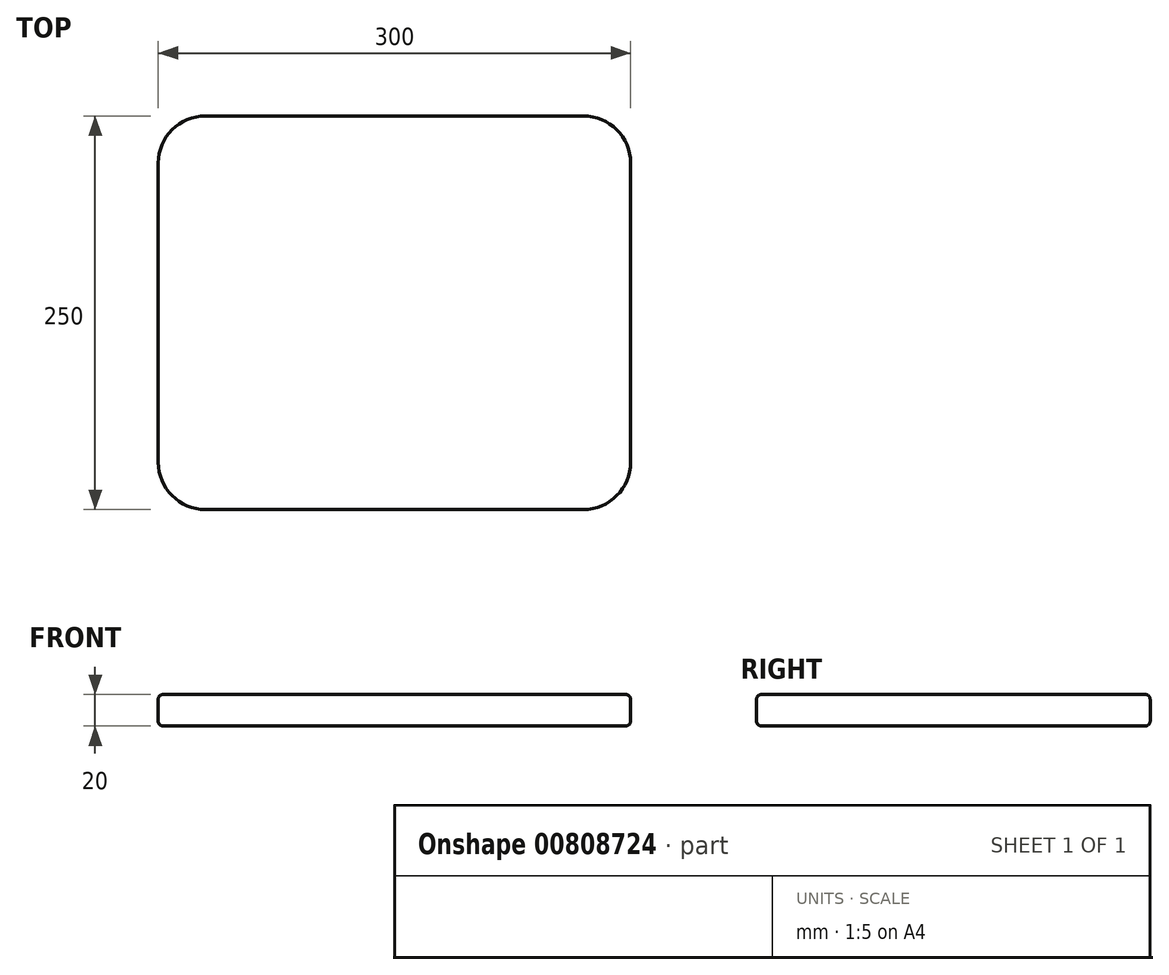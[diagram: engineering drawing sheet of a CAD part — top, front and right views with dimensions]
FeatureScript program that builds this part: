
annotation { "Feature Type Name" : "Feature", "Feature Type Description" : "" }
export const myFeature = defineFeature(function(context is Context, id is Id, definition is map)
    precondition{}
    {
        {
            var Q0;
            Q0=qCreatedBy(makeId("Top.planeOp"),FACE);
            var sketch = newSketch(context, id + "F0", { "sketchPlane" : qUnion([Q0])});
            skLineSegment(sketch, "E0.bottom", {"start": v(-113.42, 89.43) * mm, "end": v(126.58, 89.43) * mm});
            skLineSegment(sketch, "E0.top", {"start": v(-113.42, -160.57) * mm, "end": v(126.58, -160.57) * mm});
            skLineSegment(sketch, "E0.left", {"start": v(-143.42, 59.43) * mm, "end": v(-143.42, -130.57) * mm});
            skLineSegment(sketch, "E0.right", {"start": v(156.58, 59.43) * mm, "end": v(156.58, -130.57) * mm});
            skPoint(sketch, "E1.visualSharp", {"position": v(-143.42, 89.43) * mm});
            skArc(sketch, "E1.filletArc", {"start": v(-113.42, 89.43) * mm, "mid": v(-134.63, 80.65) * mm, "end": v(-143.42, 59.43) * mm});
            skPoint(sketch, "E2.visualSharp", {"position": v(156.58, 89.43) * mm});
            skArc(sketch, "E2.filletArc", {"start": v(156.58, 59.43) * mm, "mid": v(147.8, 80.65) * mm, "end": v(126.58, 89.43) * mm});
            skPoint(sketch, "E3.visualSharp", {"position": v(156.58, -160.57) * mm});
            skArc(sketch, "E3.filletArc", {"start": v(126.58, -160.57) * mm, "mid": v(147.8, -151.78) * mm, "end": v(156.58, -130.57) * mm});
            skPoint(sketch, "E4.visualSharp", {"position": v(-143.42, -160.57) * mm});
            skArc(sketch, "E4.filletArc", {"start": v(-143.42, -130.57) * mm, "mid": v(-134.63, -151.78) * mm, "end": v(-113.42, -160.57) * mm});
            skSolve(sketch);
        }
        {
            var Q0;
            Q0=makeQuery(id+"F0.imprint","IMPRINT",FACE,{"disambiguationData":[TD([[makeQuery(id+"F0.imprint","IMPRINT",EDGE,{"derivedFrom":sQuery(id+"F0.wireOp",EDGE,"E0.bottom")}),-1.0]])]});
            extrude(context, id + "F1", {"entities" : qUnion([Q0]), "depth" : 20 * mm, "offsetDistance" : 25 * mm});
        }
        {
            var Q0;
            Q0=makeQuery(id+"F1.opExtrude","CAP_FACE",FACE,{"disambiguationData":[OSD([sQuery(id+"F0.wireOp",EDGE,"E0.bottom"),sQuery(id+"F0.wireOp",EDGE,"E0.top"),sQuery(id+"F0.wireOp",EDGE,"E0.left"),sQuery(id+"F0.wireOp",EDGE,"E0.right"),sQuery(id+"F0.wireOp",EDGE,"E1.filletArc"),sQuery(id+"F0.wireOp",EDGE,"E2.filletArc"),sQuery(id+"F0.wireOp",EDGE,"E3.filletArc"),sQuery(id+"F0.wireOp",EDGE,"E4.filletArc")])],"isStart":false});
            var Q1;
            Q1=makeQuery(id+"F1.opExtrude","CAP_FACE",FACE,{"disambiguationData":[OSD([sQuery(id+"F0.wireOp",EDGE,"E0.bottom"),sQuery(id+"F0.wireOp",EDGE,"E0.top"),sQuery(id+"F0.wireOp",EDGE,"E0.left"),sQuery(id+"F0.wireOp",EDGE,"E0.right"),sQuery(id+"F0.wireOp",EDGE,"E1.filletArc"),sQuery(id+"F0.wireOp",EDGE,"E2.filletArc"),sQuery(id+"F0.wireOp",EDGE,"E3.filletArc"),sQuery(id+"F0.wireOp",EDGE,"E4.filletArc")])],"isStart":true});
            fillet(context, id + "F2", {"entities" : qUnion([Q0, Q1]), "radius" : 3 * mm, "tangentPropagation" : true, "allowEdgeOverflow" : false});
        }
        {
            var Q0;
            Q0=makeQuery(id+"F1.opExtrude","SWEPT_FACE",FACE,{"disambiguationData":[OSD([sQuery(id+"F0.wireOp",EDGE,"E0.left")])]});
            var sketch = newSketch(context, id + "F3", { "sketchPlane" : qUnion([Q0])});
            skLineSegment(sketch, "E5.0", {"start": v(-89.43, 17) * mm, "end": v(-89.43, 3) * mm, "construction": true});
            skLineSegment(sketch, "E6", {"start": v(-89.43, 10) * mm, "end": v(-59.43, 10) * mm, "construction": true});
            skLineSegment(sketch, "E7", {"start": v(-59.43, 10) * mm, "end": v(-29.43, 10) * mm, "construction": true});
            skLineSegment(sketch, "E8", {"start": v(-29.43, 10) * mm, "end": v(100.57, 10) * mm, "construction": true});
            skSolve(sketch);
        }
        {
            var Q0;
            Q0=makeQuery(id+"F1.opExtrude","SWEPT_FACE",FACE,{"disambiguationData":[OSD([sQuery(id+"F0.wireOp",EDGE,"E0.right")])]});
            var sketch = newSketch(context, id + "F4", { "sketchPlane" : qUnion([Q0])});
            skLineSegment(sketch, "E9.0", {"start": v(89.43, 10) * mm, "end": v(59.43, 10) * mm});
            skLineSegment(sketch, "E10.0", {"start": v(59.43, 10) * mm, "end": v(29.43, 10) * mm});
            skLineSegment(sketch, "E11.0", {"start": v(29.43, 10) * mm, "end": v(-100.57, 10) * mm});
            skSolve(sketch);
        }
    });
